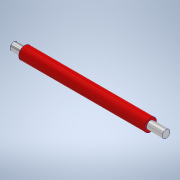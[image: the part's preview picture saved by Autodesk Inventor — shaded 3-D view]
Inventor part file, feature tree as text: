
AUTODESK INVENTOR PART (.ipt)
format: ipt  version: 2022 (Build 260153000, 153)  size: 115,200 bytes
history: native  units: in
note: dims shown in document units (in); Inventor stores cm internally (conversion verified against a paired STEP export)
features: extrude x3, sketch x3, fillet x1
ambient origin geometry x8: Origin, YZ Plane, XZ Plane, XY Plane, X Axis, Y Axis, Z Axis, Center Point
bodies: Solid1 (feature_tree)
feature tree (7):
  extrude  "Extrusion1"  Depth=1.0in TaperAngle=0.0deg
  extrude  "Extrusion2"  Depth=0.0875in TaperAngle=0.0deg
  extrude  "Extrusion3"  Depth=0.0875in TaperAngle=0.0deg
  fillet  "Fillet1"  Radius=0.0312in
  sketch  "Sketch1"  dims[d0=0.1in d1=1.0in d2=0.0in]
  sketch  "Sketch2"  dims[d3=0.0625in d4=0.0875in d5=0.0in]
  sketch  "Sketch3"  dims[d6=0.0625in d7=0.0875in d8=0.0in d9=0.0312in]
